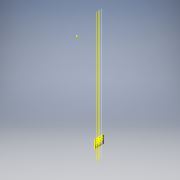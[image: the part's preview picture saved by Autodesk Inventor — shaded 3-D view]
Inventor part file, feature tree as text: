
AUTODESK INVENTOR PART (.ipt)
format: ipt  version: 2017 (Build 210142000, 142)  size: 320,512 bytes
history: native  units: in
note: dims shown in document units (in); Inventor stores cm internally (conversion verified against a paired STEP export)
features: other x8, sketch x1
ambient origin geometry x8: Origin, YZ Plane, XZ Plane, XY Plane, X Axis, Y Axis, Z Axis, Center Point
bodies: Solid1 (feature_tree)
feature tree (9):
  other  "panel_waveguide.iam"
  other  "RD-A001-P001-REV0-cutouts.ipt:1"
  other  "rj45"
  other  "waveguide"
  sketch  "Sketch5"  dims[d0=0.3937in]
  other  "Work Axis1"
  other  "Work Axis2"
  other  "Work Axis3"
  other  "Work Axis4"
